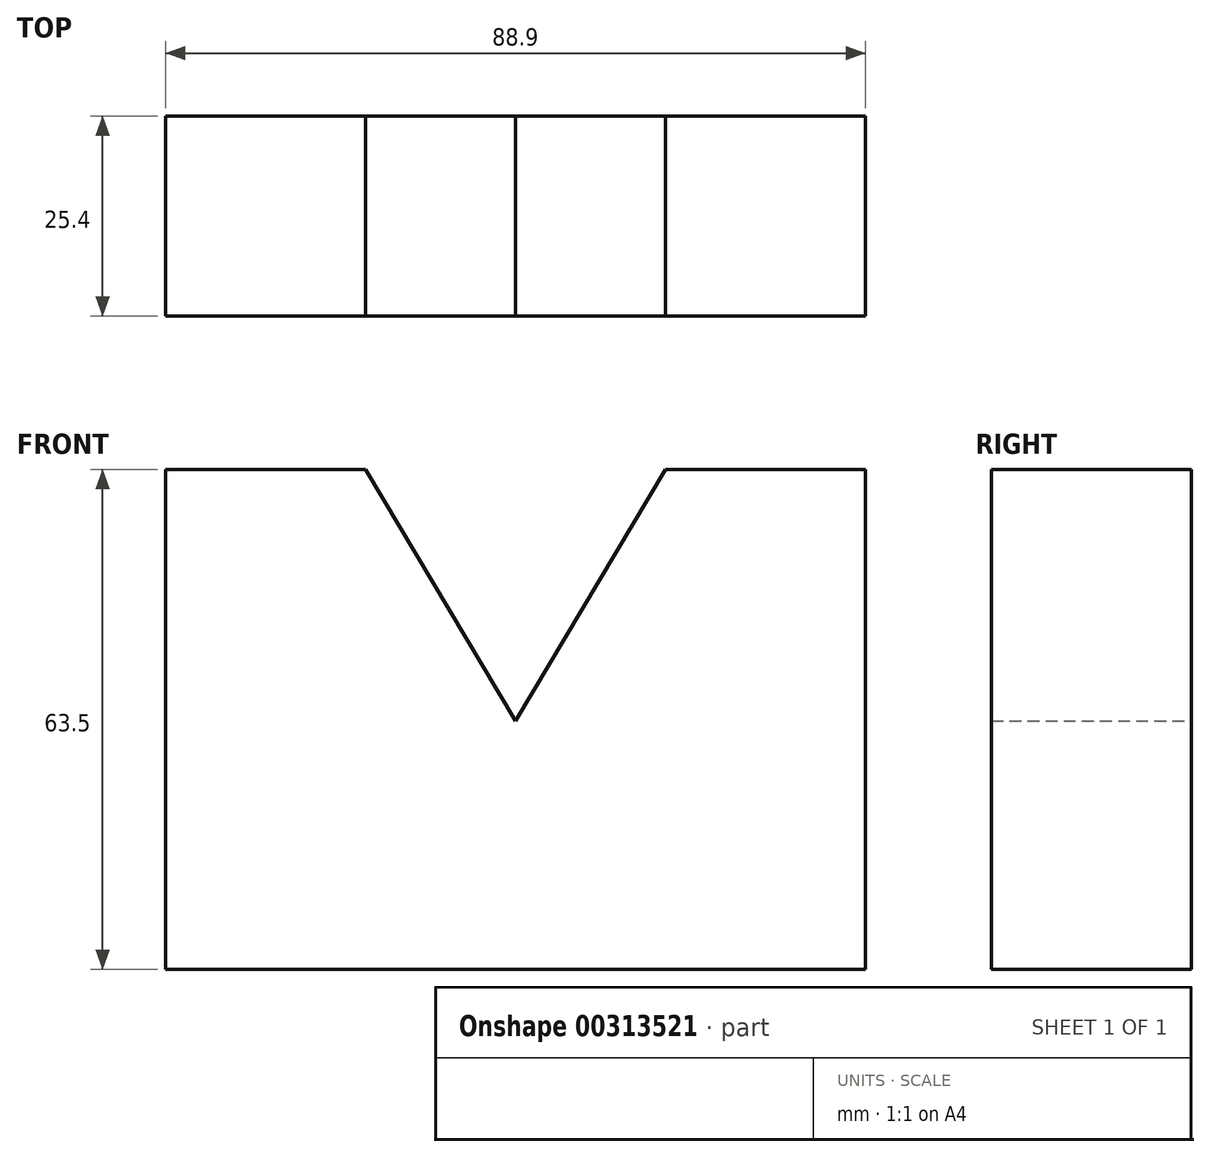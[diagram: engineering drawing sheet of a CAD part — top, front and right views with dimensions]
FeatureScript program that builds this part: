
annotation { "Feature Type Name" : "Feature", "Feature Type Description" : "" }
export const myFeature = defineFeature(function(context is Context, id is Id, definition is map)
    precondition{}
    {
        {
            var Q0;
            Q0=qCreatedBy(makeId("Front.planeOp"),FACE);
            var sketch = newSketch(context, id + "F0", { "sketchPlane" : qUnion([Q0])});
            skLineSegment(sketch, "E0", {"start": v(-40.78, 23.11) * mm, "end": v(-40.78, -40.39) * mm});
            skLineSegment(sketch, "E1", {"start": v(-40.78, -40.39) * mm, "end": v(48.12, -40.39) * mm});
            skLineSegment(sketch, "E2", {"start": v(48.12, -40.39) * mm, "end": v(48.12, 23.11) * mm});
            skLineSegment(sketch, "E3", {"start": v(48.12, 23.11) * mm, "end": v(22.72, 23.11) * mm});
            skLineSegment(sketch, "E4", {"start": v(-15.38, 23.11) * mm, "end": v(-40.78, 23.11) * mm});
            skLineSegment(sketch, "E5", {"start": v(3.67, -8.8) * mm, "end": v(-15.38, 23.11) * mm});
            skPoint(sketch, "E5.startSnap0", {"position": v(3.67, -40.39) * mm});
            skLineSegment(sketch, "E6", {"start": v(3.67, -8.8) * mm, "end": v(22.72, 23.11) * mm});
            skSolve(sketch);
        }
        {
            var Q0;
            Q0=makeQuery(id+"F0.imprint","IMPRINT",FACE,{"disambiguationData":[TD([[makeQuery(id+"F0.imprint","IMPRINT",EDGE,{"derivedFrom":sQuery(id+"F0.wireOp",EDGE,"E0")}),1.0]])]});
            extrude(context, id + "F1", {"entities" : qUnion([Q0]), "depth" : 25.4 * mm});
        }
    });
